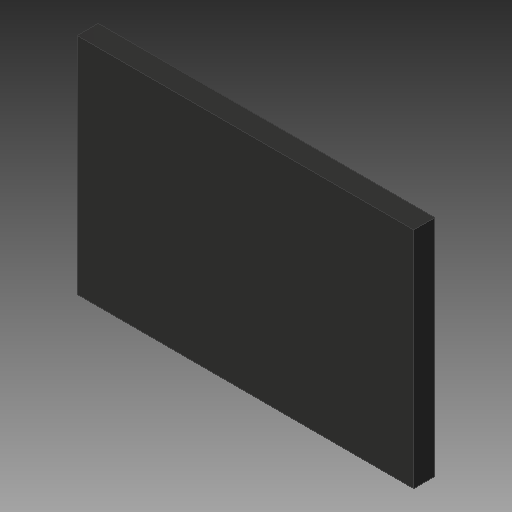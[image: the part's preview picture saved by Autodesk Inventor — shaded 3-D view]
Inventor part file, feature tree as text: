
AUTODESK INVENTOR PART (.ipt)
format: ipt  version: 2019 (Build 230136000, 136)  size: 93,696 bytes
history: native  units: mm
features: reference x8, other x3, plane x1, extrude x1, sketch x1
ambient origin geometry x8: Origin, YZ Plane, XZ Plane, XY Plane, X Axis, Y Axis, Z Axis, Center Point
bodies: Solid1 (feature_tree)
feature tree (14):
  plane  "Work Plane1"
  extrude  "Extrusion1"  Depth=9.525mm TaperAngle=0.0deg
  sketch  "Sketch1"  dims[d0=12.5mm d1=9.525mm d2=0.0mm]
  reference  "Reference1"
  reference  "Reference2"
  reference  "Reference3"
  reference  "Reference4"
  reference  "Reference5"
  reference  "Reference6"
  reference  "Reference7"
  reference  "Reference8"
  parser-record x1  (decoder bookkeeping rows leaked as tree rows — omitted from the tree; the rows remain in map.json)
  other  "speaker_assembly_v2.iam"
  other  "BA4-Solidworks:1"
note: 1 file-system path scrubbed to <path> (originals preserved in map.json)
